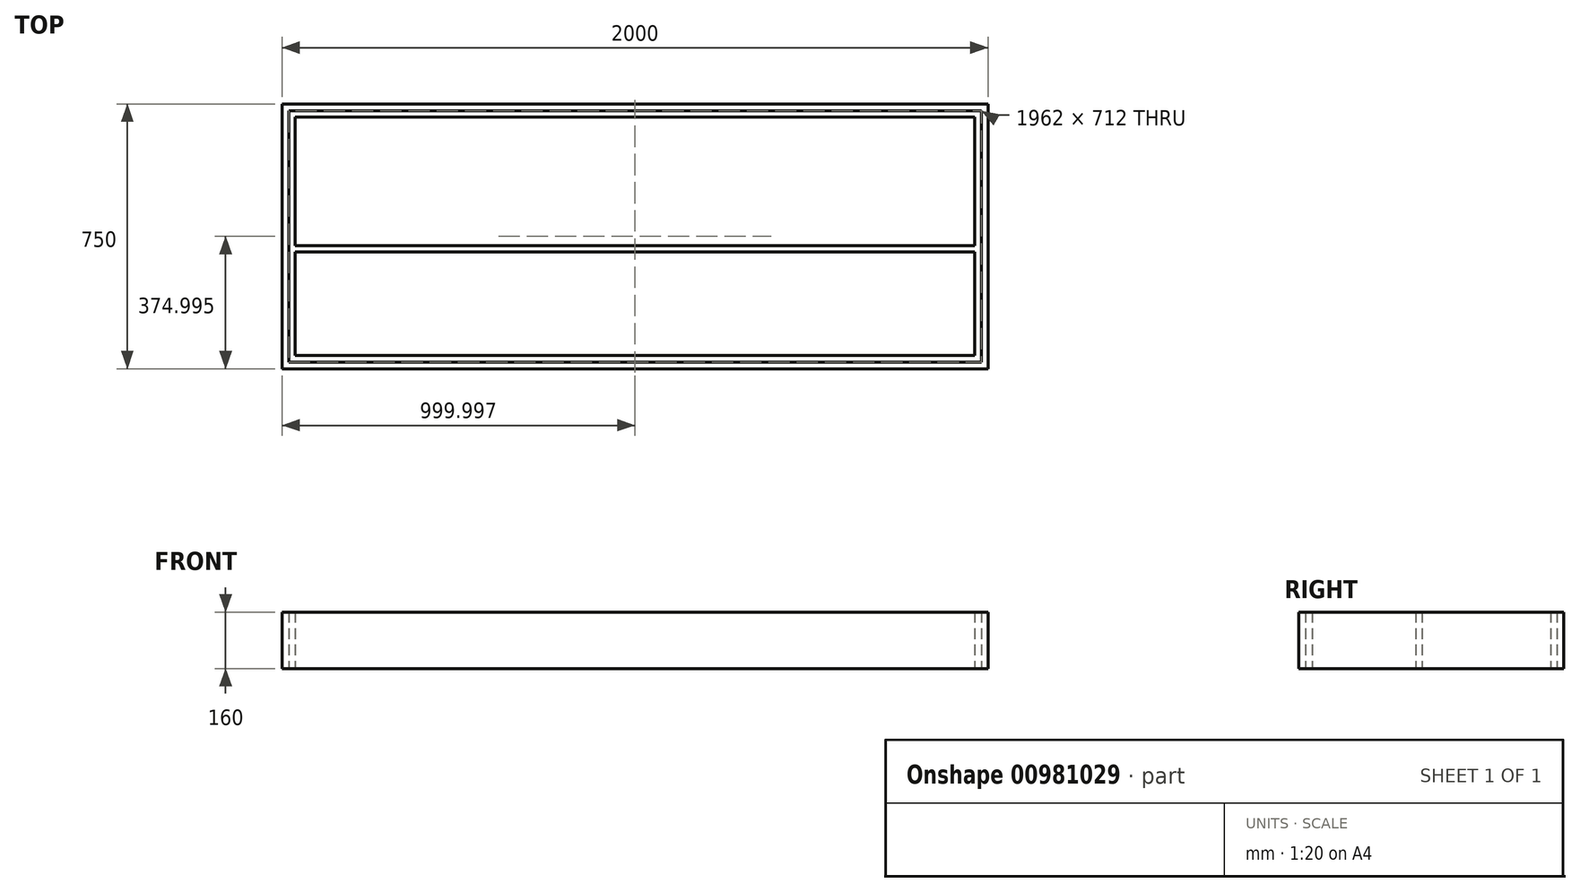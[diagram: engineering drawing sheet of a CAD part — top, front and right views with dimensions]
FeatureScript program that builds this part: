
annotation { "Feature Type Name" : "Feature", "Feature Type Description" : "" }
export const myFeature = defineFeature(function(context is Context, id is Id, definition is map)
    precondition{}
    {
        {
            var Q0;
            Q0=qCreatedBy(makeId("Top.planeOp"),FACE);
            var sketch = newSketch(context, id + "F0", { "sketchPlane" : qUnion([Q0])});
            skLineSegment(sketch, "E0.bottom", {"start": v(-1009.36, 191.64) * mm, "end": v(990.64, 191.64) * mm});
            skLineSegment(sketch, "E0.top", {"start": v(-1009.36, -558.36) * mm, "end": v(990.64, -558.36) * mm});
            skLineSegment(sketch, "E0.left", {"start": v(-1009.36, 191.64) * mm, "end": v(-1009.36, -558.36) * mm});
            skLineSegment(sketch, "E0.right", {"start": v(990.64, 191.64) * mm, "end": v(990.64, -558.36) * mm});
            skLineSegment(sketch, "E1.bottom", {"start": v(-990.36, 172.64) * mm, "end": v(971.64, 172.64) * mm});
            skLineSegment(sketch, "E1.top", {"start": v(-990.36, -539.36) * mm, "end": v(971.64, -539.36) * mm});
            skLineSegment(sketch, "E1.left", {"start": v(-990.36, 172.64) * mm, "end": v(-990.36, -539.36) * mm});
            skLineSegment(sketch, "E1.right", {"start": v(971.64, 172.64) * mm, "end": v(971.64, -539.36) * mm});
            skLineSegment(sketch, "E2", {"start": v(-1009.36, 191.64) * mm, "end": v(-990.36, 172.64) * mm});
            skLineSegment(sketch, "E3", {"start": v(-1009.36, -558.36) * mm, "end": v(-990.36, -539.36) * mm});
            skLineSegment(sketch, "E4", {"start": v(971.64, -539.36) * mm, "end": v(990.64, -558.36) * mm});
            skLineSegment(sketch, "E5", {"start": v(990.64, 191.64) * mm, "end": v(971.64, 172.64) * mm});
            skLineSegment(sketch, "E6.bottom", {"start": v(-990.36, 172.64) * mm, "end": v(-972.36, 172.64) * mm});
            skLineSegment(sketch, "E6.top", {"start": v(-990.36, -539.36) * mm, "end": v(-972.36, -539.36) * mm});
            skLineSegment(sketch, "E6.right", {"start": v(-972.36, 172.64) * mm, "end": v(-972.36, -539.36) * mm});
            skLineSegment(sketch, "E7.bottom", {"start": v(971.64, 172.64) * mm, "end": v(953.64, 172.64) * mm});
            skLineSegment(sketch, "E7.top", {"start": v(971.64, -539.36) * mm, "end": v(953.64, -539.36) * mm});
            skLineSegment(sketch, "E7.right", {"start": v(953.64, 172.64) * mm, "end": v(953.64, -539.36) * mm});
            skLineSegment(sketch, "E8.bottom", {"start": v(-972.36, 172.64) * mm, "end": v(953.64, 172.64) * mm});
            skLineSegment(sketch, "E8.top", {"start": v(-972.36, 154.64) * mm, "end": v(953.64, 154.64) * mm});
            skLineSegment(sketch, "E8.left", {"start": v(-972.36, 172.64) * mm, "end": v(-972.36, 154.64) * mm});
            skLineSegment(sketch, "E8.right", {"start": v(953.64, 172.64) * mm, "end": v(953.64, 154.64) * mm});
            skLineSegment(sketch, "E9.bottom", {"start": v(-972.36, -539.36) * mm, "end": v(953.64, -539.36) * mm});
            skLineSegment(sketch, "E9.top", {"start": v(-972.36, -521.36) * mm, "end": v(953.64, -521.36) * mm});
            skLineSegment(sketch, "E9.left", {"start": v(-972.36, -539.36) * mm, "end": v(-972.36, -521.36) * mm});
            skLineSegment(sketch, "E9.right", {"start": v(953.64, -539.36) * mm, "end": v(953.64, -521.36) * mm});
            skLineSegment(sketch, "E10.bottom", {"start": v(-972.36, -209.8) * mm, "end": v(953.64, -209.8) * mm});
            skLineSegment(sketch, "E10.top", {"start": v(-972.36, -227.8) * mm, "end": v(953.64, -227.8) * mm});
            skLineSegment(sketch, "E10.left", {"start": v(-972.36, -209.8) * mm, "end": v(-972.36, -227.8) * mm});
            skLineSegment(sketch, "E10.right", {"start": v(953.64, -209.8) * mm, "end": v(953.64, -227.8) * mm});
            skSolve(sketch);
        }
        {
            var Q0;
            {var subQ0=sQuery(id+"F0.wireOp",EDGE,"E8.top");Q0=makeQuery(id+"F0.imprint","IMPRINT",FACE,{"disambiguationData":[TD([[makeQuery(id+"F0.imprint","IMPRINT",EDGE,{"derivedFrom":subQ0}),-1.0]])]});}
            var Q1;
            {var subQ0=sQuery(id+"F0.wireOp",EDGE,"E9.top");Q1=makeQuery(id+"F0.imprint","IMPRINT",FACE,{"disambiguationData":[TD([[makeQuery(id+"F0.imprint","IMPRINT",EDGE,{"derivedFrom":subQ0}),1.0]])]});}
            var Q2;
            Q2=makeQuery(id+"F0.imprint","IMPRINT",FACE,{"disambiguationData":[TD([[makeQuery(id+"F0.imprint","IMPRINT",EDGE,{"derivedFrom":sQuery(id+"F0.wireOp",EDGE,"E0.bottom")}),-1.0]])]});
            extrude(context, id + "F1", {"entities" : qUnion([Q0, Q1, Q2]), "depth" : 160 * mm, "offsetDistance" : 25 * mm});
        }
        {
            var Q0;
            Q0 = qSketchRegion(id + "F0", true);
            extrude(context, id + "F2", {"entities" : qUnion([Q0]), "operationType" : NewBodyOperationType.ADD, "depth" : 160 * mm, "offsetDistance" : 25 * mm});
        }
    });
